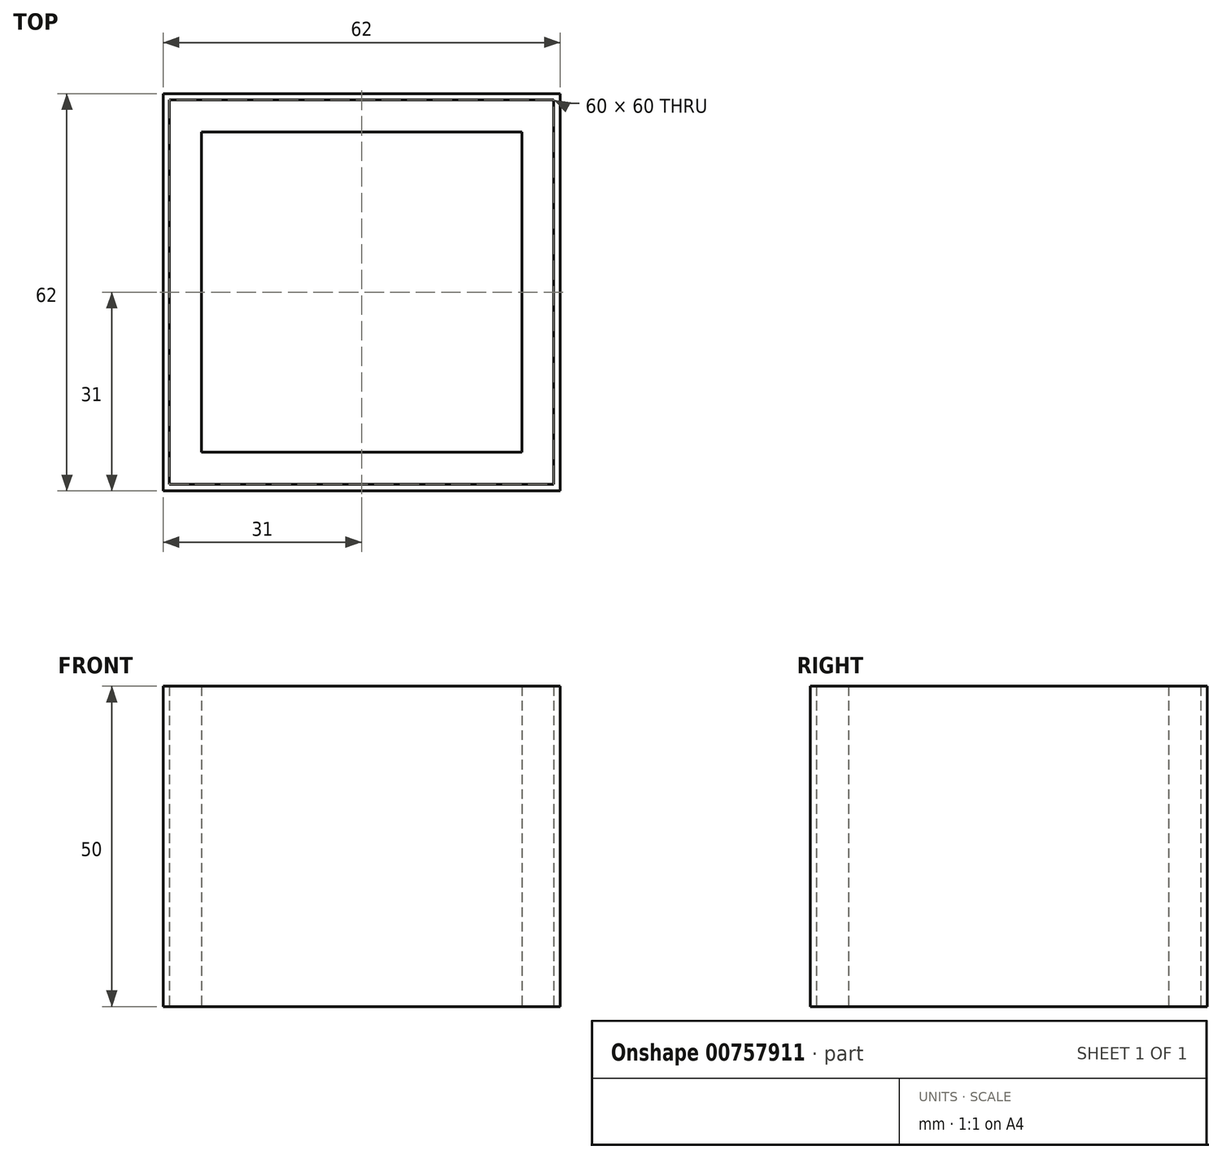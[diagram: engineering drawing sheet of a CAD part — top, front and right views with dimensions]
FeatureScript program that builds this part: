
annotation { "Feature Type Name" : "Feature", "Feature Type Description" : "" }
export const myFeature = defineFeature(function(context is Context, id is Id, definition is map)
    precondition{}
    {
        {
            var Q0;
            Q0=qCreatedBy(makeId("Top.planeOp"),FACE);
            var sketch = newSketch(context, id + "F0", { "sketchPlane" : qUnion([Q0])});
            skLineSegment(sketch, "E0.bottom", {"start": v(0, 0) * mm, "end": v(50, 0) * mm});
            skLineSegment(sketch, "E0.top", {"start": v(0, -50) * mm, "end": v(50, -50) * mm});
            skLineSegment(sketch, "E0.left", {"start": v(0, 0) * mm, "end": v(0, -50) * mm});
            skLineSegment(sketch, "E0.right", {"start": v(50, 0) * mm, "end": v(50, -50) * mm});
            skLineSegment(sketch, "E1.bottom", {"start": v(55, -55) * mm, "end": v(-5, -55) * mm});
            skLineSegment(sketch, "E1.top", {"start": v(55, 5) * mm, "end": v(-5, 5) * mm});
            skLineSegment(sketch, "E1.left", {"start": v(55, -55) * mm, "end": v(55, 5) * mm});
            skLineSegment(sketch, "E1.right", {"start": v(-5, -55) * mm, "end": v(-5, 5) * mm});
            skPoint(sketch, "E1.middle", {"position": v(25, -25) * mm});
            skLineSegment(sketch, "E2.bottom", {"start": v(56, -56) * mm, "end": v(-6, -56) * mm});
            skLineSegment(sketch, "E2.top", {"start": v(56, 6) * mm, "end": v(-6, 6) * mm});
            skLineSegment(sketch, "E2.left", {"start": v(56, -56) * mm, "end": v(56, 6) * mm});
            skLineSegment(sketch, "E2.right", {"start": v(-6, -56) * mm, "end": v(-6, 6) * mm});
            skSolve(sketch);
        }
        {
            var Q0;
            Q0=makeQuery(id+"F0.imprint","IMPRINT",FACE,{"disambiguationData":[TD([[makeQuery(id+"F0.imprint","IMPRINT",EDGE,{"derivedFrom":sQuery(id+"F0.wireOp",EDGE,"E0.bottom")}),-1.0]])]});
            extrude(context, id + "F1", {"entities" : qUnion([Q0]), "depth" : 50 * mm, "offsetDistance" : 25 * mm});
        }
        {
            var Q0;
            Q0=makeQuery(id+"F0.imprint","IMPRINT",FACE,{"disambiguationData":[TD([[makeQuery(id+"F0.imprint","IMPRINT",EDGE,{"derivedFrom":sQuery(id+"F0.wireOp",EDGE,"E1.bottom")}),1.0]])]});
            extrude(context, id + "F2", {"entities" : qUnion([Q0]), "depth" : 50 * mm, "offsetDistance" : 25 * mm});
        }
    });
